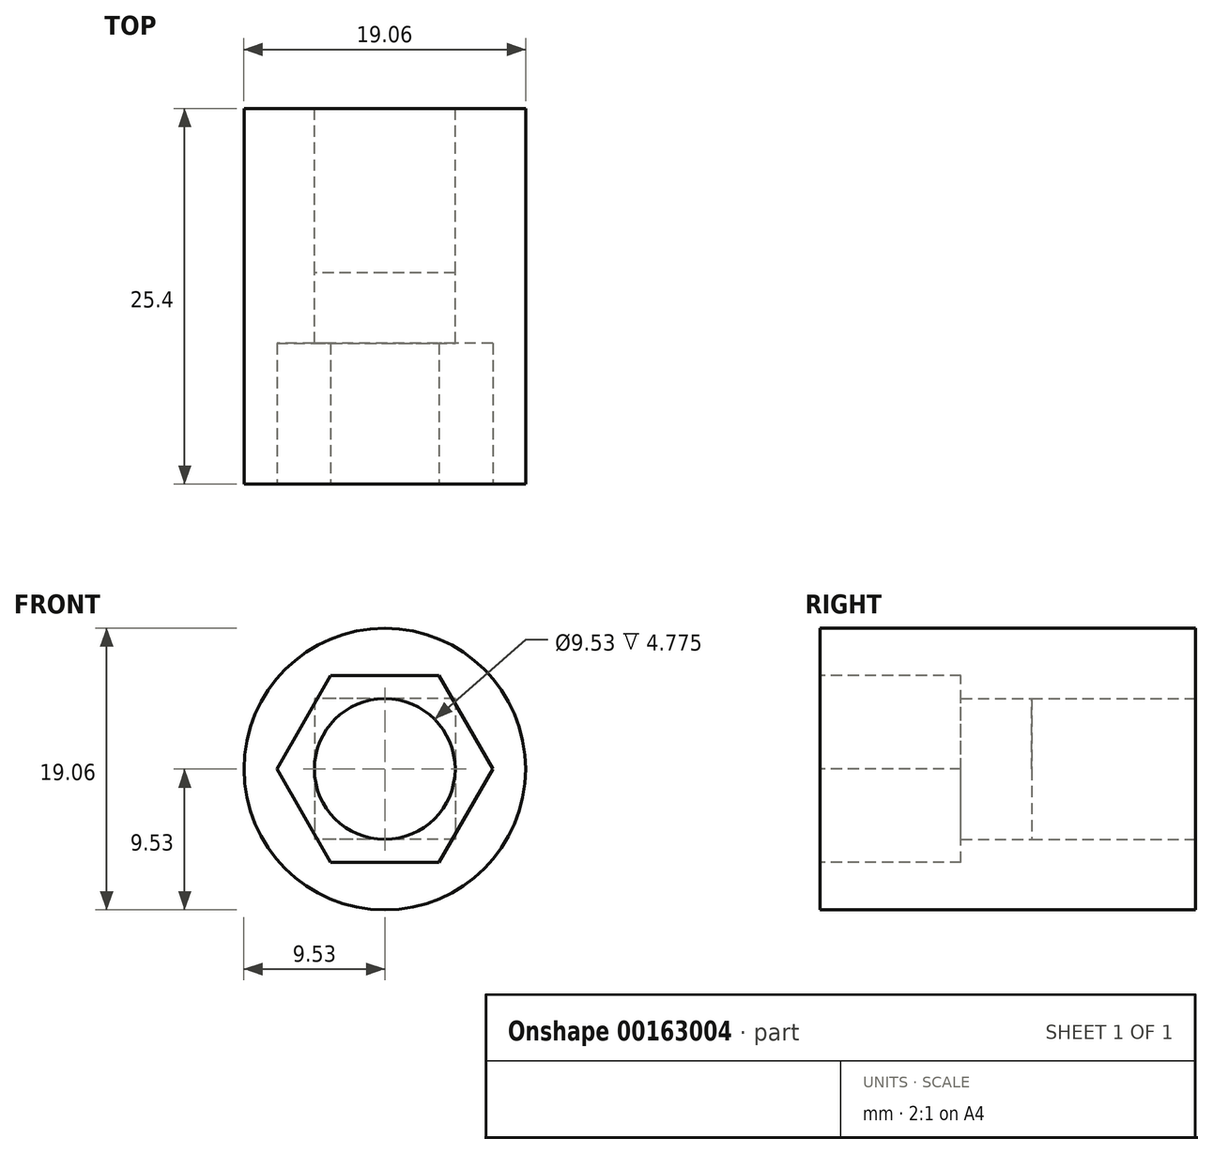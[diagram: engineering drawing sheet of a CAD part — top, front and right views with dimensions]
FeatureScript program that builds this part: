
annotation { "Feature Type Name" : "Feature", "Feature Type Description" : "" }
export const myFeature = defineFeature(function(context is Context, id is Id, definition is map)
    precondition{}
    {
        {
            var Q0;
            Q0=qCreatedBy(makeId("Front.planeOp"),FACE);
            var sketch = newSketch(context, id + "F0", { "sketchPlane" : qUnion([Q0])});
            skCircle(sketch, "E0", {"center": v(0, 0) * mm, "radius": 9.53 * mm});
            skSolve(sketch);
        }
        {
            var Q0;
            Q0 = qSketchRegion(id + "F0", true);
            extrude(context, id + "F1", {"entities" : qUnion([Q0]), "depth" : 25.4 * mm});
        }
        {
            var Q0;
            Q0=qCreatedBy(makeId("Front.planeOp"),FACE);
            var sketch = newSketch(context, id + "F2", { "sketchPlane" : qUnion([Q0])});
            skLineSegment(sketch, "E1.bottom", {"start": v(4.76, 4.76) * mm, "end": v(-4.76, 4.76) * mm});
            skLineSegment(sketch, "E1.top", {"start": v(4.76, -4.76) * mm, "end": v(-4.76, -4.76) * mm});
            skLineSegment(sketch, "E1.left", {"start": v(4.76, 4.76) * mm, "end": v(4.76, -4.76) * mm});
            skLineSegment(sketch, "E1.right", {"start": v(-4.76, 4.76) * mm, "end": v(-4.76, -4.76) * mm});
            skPoint(sketch, "E1.middle", {"position": v(0, 0) * mm});
            skCircle(sketch, "E2", {"center": v(0, 0) * mm, "radius": 4.76 * mm});
            skSolve(sketch);
        }
        {
            var Q0;
            Q0=qCreatedBy(makeId("Front.planeOp"),FACE);
            var sketch = newSketch(context, id + "F3", { "sketchPlane" : qUnion([Q0])});
            skSolve(sketch);
        }
        {
            var Q0;
            Q0 = qSketchRegion(id + "F3", true);
            var Q1;
            {var subQ0=sQuery(id+"F2.wireOp",EDGE,"E2");var subQ1=makeQuery(id+"F2.imprint","INTERSECT",VERTEX,{"derivedFrom":[sQuery(id+"F2.wireOp",EDGE,"E1.bottom"),subQ0]});Q1=makeQuery(id+"F2.imprint","IMPRINT",FACE,{"disambiguationData":[TD([[makeQuery(id+"F2.imprint","IMPRINT",EDGE,{"disambiguationData":[TD([[subQ1,1.0]])],"derivedFrom":subQ0}),1.0]])]});}
            extrude(context, id + "F4", {"entities" : qUnion([Q0, Q1]), "operationType" : NewBodyOperationType.REMOVE, "endBound" : BoundingType.THROUGH_ALL, "oppositeDirection" : true, "depth" : 25.4 * mm});
        }
        {
            var Q0;
            Q0=qCreatedBy(makeId("Front.planeOp"),FACE);
            var sketch = newSketch(context, id + "F5", { "sketchPlane" : qUnion([Q0])});
            skLineSegment(sketch, "E3.bottom", {"start": v(-4.76, 4.76) * mm, "end": v(4.76, 4.76) * mm});
            skLineSegment(sketch, "E3.top", {"start": v(-4.76, -4.76) * mm, "end": v(4.76, -4.76) * mm});
            skLineSegment(sketch, "E3.left", {"start": v(-4.76, 4.76) * mm, "end": v(-4.76, -4.76) * mm});
            skLineSegment(sketch, "E3.right", {"start": v(4.76, 4.76) * mm, "end": v(4.76, -4.76) * mm});
            skPoint(sketch, "E3.middle", {"position": v(0, 0) * mm});
            skCircle(sketch, "E4", {"center": v(0, 0) * mm, "radius": 4.76 * mm});
            skSolve(sketch);
        }
        {
            var Q0;
            {var subQ0=sQuery(id+"F5.wireOp",EDGE,"E4");var subQ1=makeQuery(id+"F5.imprint","INTERSECT",VERTEX,{"derivedFrom":[sQuery(id+"F5.wireOp",EDGE,"E3.bottom"),subQ0]});Q0=makeQuery(id+"F5.imprint","IMPRINT",FACE,{"disambiguationData":[TD([[makeQuery(id+"F5.imprint","IMPRINT",EDGE,{"disambiguationData":[TD([[subQ1,1.0]])],"derivedFrom":subQ0}),1.0]])]});}
            extrude(context, id + "F6", {"entities" : qUnion([Q0]), "operationType" : NewBodyOperationType.REMOVE, "endBound" : BoundingType.THROUGH_ALL, "oppositeDirection" : true, "depth" : 25.4 * mm});
        }
        {
            var Q0;
            Q0=qCreatedBy(makeId("Front.planeOp"),FACE);
            var sketch = newSketch(context, id + "F7", { "sketchPlane" : qUnion([Q0])});
            skLineSegment(sketch, "E5.bottom", {"start": v(4.76, 4.76) * mm, "end": v(-4.76, 4.76) * mm});
            skLineSegment(sketch, "E5.top", {"start": v(4.76, -4.76) * mm, "end": v(-4.76, -4.76) * mm});
            skLineSegment(sketch, "E5.left", {"start": v(4.76, 4.76) * mm, "end": v(4.76, -4.76) * mm});
            skLineSegment(sketch, "E5.right", {"start": v(-4.76, 4.76) * mm, "end": v(-4.76, -4.76) * mm});
            skPoint(sketch, "E5.middle", {"position": v(0, 0) * mm});
            skCircle(sketch, "E6", {"center": v(0, 0) * mm, "radius": 4.76 * mm});
            skSolve(sketch);
        }
        {
            var Q0;
            {var subQ0=sQuery(id+"F7.wireOp",EDGE,"E6");var subQ1=makeQuery(id+"F7.imprint","INTERSECT",VERTEX,{"derivedFrom":[sQuery(id+"F7.wireOp",EDGE,"E5.bottom"),subQ0]});Q0=makeQuery(id+"F7.imprint","IMPRINT",FACE,{"disambiguationData":[TD([[makeQuery(id+"F7.imprint","IMPRINT",EDGE,{"disambiguationData":[TD([[subQ1,1.0]])],"derivedFrom":subQ0}),1.0]])]});}
            extrude(context, id + "F8", {"entities" : qUnion([Q0]), "operationType" : NewBodyOperationType.REMOVE, "endBound" : BoundingType.THROUGH_ALL, "depth" : 25.4 * mm});
        }
        {
            var Q0;
            Q0 = qSketchRegion(id + "F7", true);
            extrude(context, id + "F9", {"entities" : qUnion([Q0]), "operationType" : NewBodyOperationType.REMOVE, "depth" : 11.1 * mm});
        }
        {
            var Q0;
            Q0=makeQuery(id+"F1.opExtrude","CAP_FACE",FACE,{"disambiguationData":[OSD([sQuery(id+"F0.wireOp",EDGE,"E0")])],"isStart":false});
            var sketch = newSketch(context, id + "F10", { "sketchPlane" : qUnion([Q0])});
            skCircle(sketch, "E7.cCircle", {"center": v(0, 0) * mm, "radius": 6.32 * mm, "construction": true});
            skLineSegment(sketch, "E7.0", {"start": v(-3.65, 6.32) * mm, "end": v(3.65, 6.32) * mm});
            skLineSegment(sketch, "E7.1", {"start": v(3.65, 6.32) * mm, "end": v(7.3, 0) * mm});
            skLineSegment(sketch, "E7.2", {"start": v(7.3, 0) * mm, "end": v(3.65, -6.32) * mm});
            skLineSegment(sketch, "E7.3", {"start": v(3.65, -6.32) * mm, "end": v(-3.65, -6.32) * mm});
            skLineSegment(sketch, "E7.4", {"start": v(-3.65, -6.32) * mm, "end": v(-7.3, 0) * mm});
            skLineSegment(sketch, "E7.5", {"start": v(-7.3, 0) * mm, "end": v(-3.65, 6.32) * mm});
            skPoint(sketch, "E7.0.midPoint", {"position": v(0, 6.32) * mm});
            skSolve(sketch);
        }
        {
            var Q0;
            Q0 = qSketchRegion(id + "F10", true);
            extrude(context, id + "F11", {"entities" : qUnion([Q0]), "operationType" : NewBodyOperationType.REMOVE, "oppositeDirection" : true, "depth" : 9.52 * mm});
        }
    });
